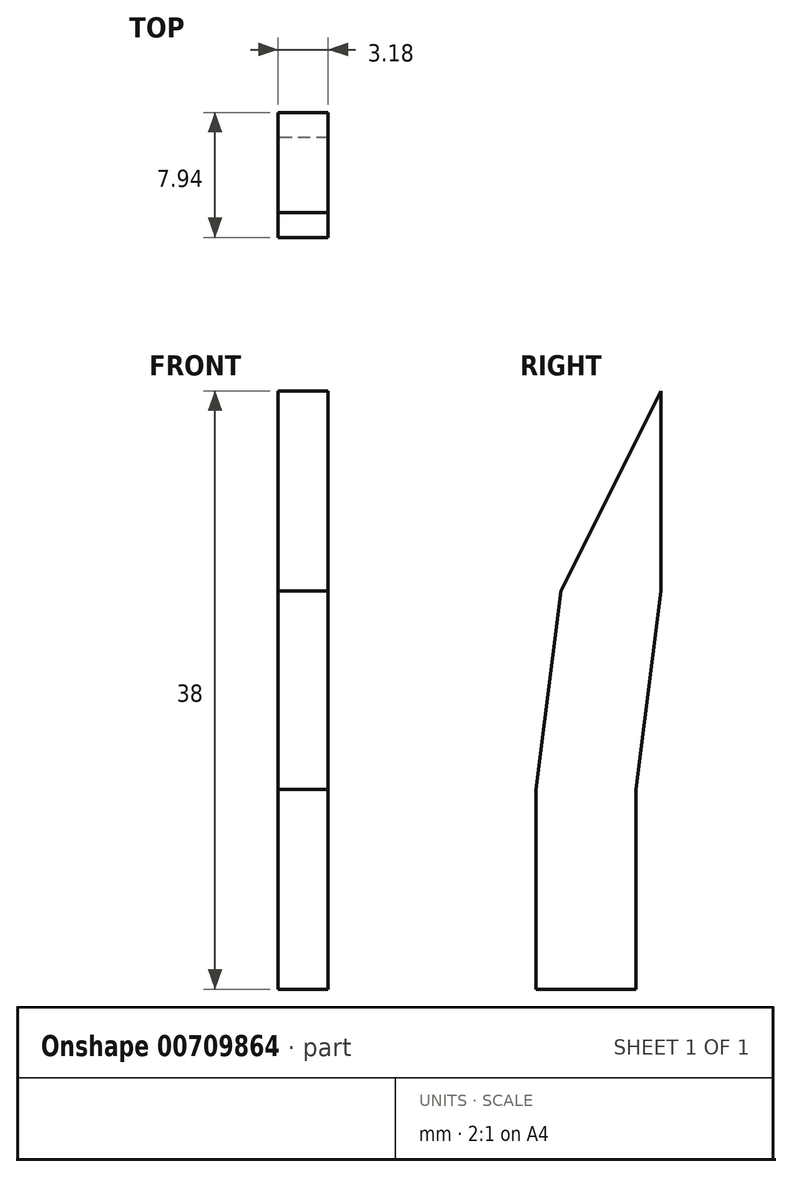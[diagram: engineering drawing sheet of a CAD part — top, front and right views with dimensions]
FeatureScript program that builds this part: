
annotation { "Feature Type Name" : "Feature", "Feature Type Description" : "" }
export const myFeature = defineFeature(function(context is Context, id is Id, definition is map)
    precondition{}
    {
        {
            var Q0;
            Q0=qCreatedBy(makeId("Right.planeOp"),FACE);
            var sketch = newSketch(context, id + "F0", { "sketchPlane" : qUnion([Q0])});
            skLineSegment(sketch, "E0.bottom", {"start": v(-3.18, 6.35) * mm, "end": v(3.17, 6.35) * mm});
            skLineSegment(sketch, "E0.top", {"start": v(-3.18, -6.35) * mm, "end": v(3.18, -6.35) * mm});
            skLineSegment(sketch, "E0.left", {"start": v(-3.17, 6.35) * mm, "end": v(-3.18, -6.35) * mm});
            skLineSegment(sketch, "E0.right", {"start": v(3.17, 6.35) * mm, "end": v(3.18, -6.35) * mm});
            skLineSegment(sketch, "E1", {"start": v(-3.18, 6.35) * mm, "end": v(-1.59, 18.95) * mm});
            skLineSegment(sketch, "E2", {"start": v(3.17, 6.35) * mm, "end": v(4.76, 18.95) * mm});
            skLineSegment(sketch, "E3", {"start": v(4.76, 18.95) * mm, "end": v(4.76, 31.65) * mm});
            skLineSegment(sketch, "E4", {"start": v(4.76, 31.65) * mm, "end": v(-1.59, 18.95) * mm});
            skSolve(sketch);
        }
        {
            var Q0;
            Q0=makeQuery(id+"F0.imprint","IMPRINT",FACE,{"disambiguationData":[TD([[makeQuery(id+"F0.imprint","IMPRINT",EDGE,{"derivedFrom":sQuery(id+"F0.wireOp",EDGE,"E0.bottom")}),1.0]])]});
            var Q1;
            Q1=makeQuery(id+"F0.imprint","IMPRINT",FACE,{"disambiguationData":[TD([[makeQuery(id+"F0.imprint","IMPRINT",EDGE,{"derivedFrom":sQuery(id+"F0.wireOp",EDGE,"E0.bottom")}),-1.0]])]});
            extrude(context, id + "F1", {"entities" : qUnion([Q0, Q1]), "endBound" : BoundingType.SYMMETRIC, "depth" : 3.17 * mm, "offsetDistance" : 25.4 * mm});
        }
    });
